# Revit family: PGR_Noken_WCAssmbly_NK-Concept-WH
name_source: partatom
category: Plumbing Fixtures
revit_build: Autodesk Revit 2017 (Build: 20171027_0315(x64)
units: mm (PartAtom-declared; Revit-internal decimal feet)

## family parameters
Always vertical = Yes
Cut with Voids When Loaded = No
Host = Wall
OmniClass Number = 23.45.05.14.31
OmniClass Title = Combination Toilets
Part Type = Normal
Room Calculation Point = No
Round Connector Dimension = Use Diameter
Shared = Yes

## types (1)
- NK-Concept-100160818
    AccessibilityPerformance = See ProductInformation for technical PDF
    AssetType = Fixed
    BIMObjectName = PGR_Noken_WCAssembly_NK_Concept_White-375x535mm-100160818
    CWFU = 0
    Category = Ss_40_15_90_97: WC systems
    CertificationApprovalCompany1 = Kiwa UK
    CertificationApprovalCompany2 = Eco
    CisternMountingType = Rear inlet
    CodePerformance = EN 997 , EN 33
    Collection = NK Concept
    Color = White
    Description = Nk concept wall hung pan with fixing kit. Flushing 4,5-3 L . Made in Vitreous China. Complies with the standards EN 997 and EN 33. 10 years warranty. KIWA UK certified (certificate number 1609727)
    DiameterCW = 55 mm
    DrainSize = 102 mm
    DurationUnit = year
    Features = See ProductInformation for technical PDF
    Finish = White
    FlushRate = 3/4.5L
    IfcExportAs = IfcSanitaryTerminalType
    IfcExportType = ToiletPan
    ManufacturerURL = www.noken.com
    Material = Porcelain
    MaterialCeramic = PGR_Noken_Porcelain_White
    MaterialPlastic = PGR_Noken_Thermodur_White
    Model = 100160818
    ModelNumber = 100160818
    ModelReference = INODORO NK CONCEPT SUSPENDIDO
    NBSDescription = WC assembly
    NBSReference = 35-70-70/134
    Name = WCAssembly_NK_Concept_White-375x535mm-100160818
    NettWeight = 28.1
    NominalDepth = 0 mm  [stored 0 ft]
    NominalHeight = 0 mm  [stored 0 ft]
    NominalLength = 535 mm  [stored 1.75525 ft]
    NominalWidth = 375 mm  [stored 1.23031 ft]
    PanColor = White
    PanMaterial = Porcelain
    PanMounting = Wall hung
    ProductInformation = http://www.noken.com
    Reference = -
    SeatCodePerformance = XPD 12-207
    SeatColor = White
    SeatHasCover = Yes
    SeatMaterial = Thermodur
    SeatNominalHeight = 50 mm  [stored 0.164042 ft]
    SeatNominalLength = 440 mm  [stored 1.44357 ft]
    SeatNominalWidth = 375 mm  [stored 1.23031 ft]
    SeatType = RingSeat
    Size = 375x535 mm
    SpilloverLevel = 0 mm  [stored 0 ft]
    Status = UNSET
    SustainabilityPerformance = See ProductInformation for technical PDF
    TechnicalDrawing = See ProductInformation for technical PDF
    ToiletType = WC wall-hung
    Type Image = 100160818.jpg
    URL = www.noken.com
    Uniclass2015Code = Ss_40_15_90_97
    Uniclass2015Title = WC systems
    Uniclass2015Version = v1_8
    Version = 1
    WFU = 0
    WarrantyDescription = See ProductInformation for technical PDF
    WarrantyDurationUnit = year
    WaterInletType = Concealed
    WaterOutletType = From the wall

note: [stored X ft] marks values corroborated as IEEE doubles in the binary element streams (Revit-internal decimal feet)

## geometry (parser evidence)
native form markers: Blend x2
no freeform markers — native parametric forms only
